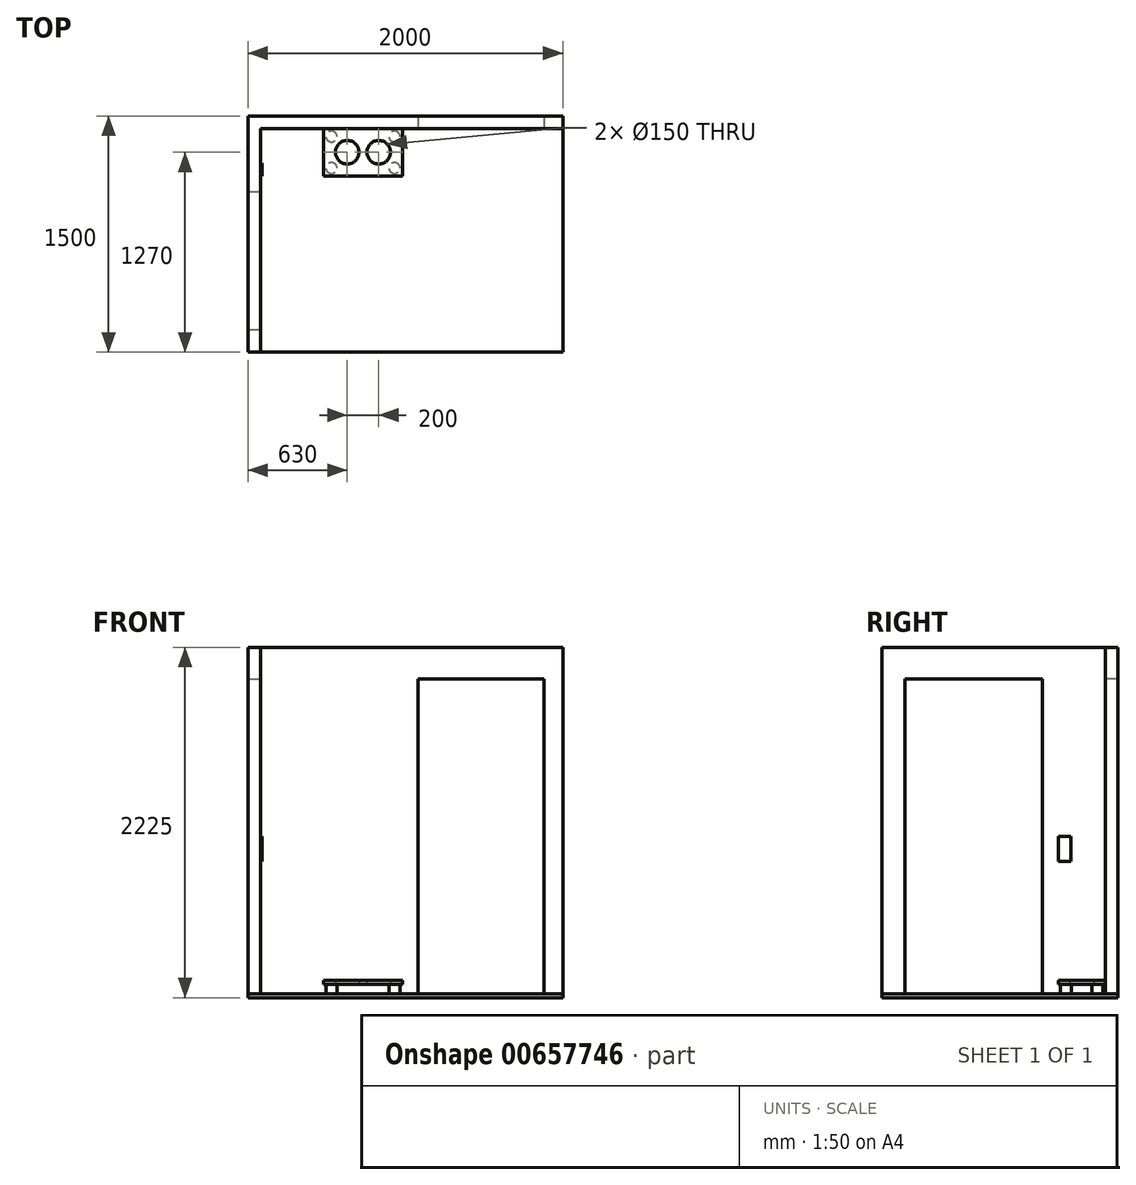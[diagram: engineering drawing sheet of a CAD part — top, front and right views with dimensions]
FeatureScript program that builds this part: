
annotation { "Feature Type Name" : "Feature", "Feature Type Description" : "" }
export const myFeature = defineFeature(function(context is Context, id is Id, definition is map)
    precondition{}
    {
        {
            var Q0;
            Q0=qCreatedBy(makeId("Top.planeOp"),FACE);
            var sketch = newSketch(context, id + "F0", { "sketchPlane" : qUnion([Q0])});
            skLineSegment(sketch, "E0.bottom", {"start": v(-1000, 1500) * mm, "end": v(1000, 1500) * mm});
            skLineSegment(sketch, "E0.top", {"start": v(-1000, 0) * mm, "end": v(1000, 0) * mm});
            skLineSegment(sketch, "E0.left", {"start": v(-1000, 1500) * mm, "end": v(-1000, 0) * mm});
            skLineSegment(sketch, "E0.right", {"start": v(1000, 1500) * mm, "end": v(1000, 0) * mm});
            skSolve(sketch);
        }
        {
            var Q0;
            Q0 = qSketchRegion(id + "F0", true);
            extrude(context, id + "F1", {"entities" : qUnion([Q0]), "depth" : 25 * mm, "offsetDistance" : 25 * mm});
        }
        {
            var Q0;
            Q0=makeQuery(id+"F1.opExtrude","CAP_FACE",FACE,{"disambiguationData":[OSD([sQuery(id+"F0.wireOp",EDGE,"E0.bottom"),sQuery(id+"F0.wireOp",EDGE,"E0.top"),sQuery(id+"F0.wireOp",EDGE,"E0.left"),sQuery(id+"F0.wireOp",EDGE,"E0.right")])],"isStart":false});
            var sketch = newSketch(context, id + "F2", { "sketchPlane" : qUnion([Q0])});
            skLineSegment(sketch, "E1", {"start": v(-1000, 0) * mm, "end": v(-1000, 1500) * mm});
            skLineSegment(sketch, "E2", {"start": v(-1000, 1500) * mm, "end": v(1000, 1500) * mm});
            skLineSegment(sketch, "E3", {"start": v(1000, 1500) * mm, "end": v(1000, 1420) * mm});
            skLineSegment(sketch, "E4", {"start": v(1000, 1420) * mm, "end": v(-920, 1420) * mm});
            skLineSegment(sketch, "E5", {"start": v(-920, 1420) * mm, "end": v(-920, 0) * mm});
            skLineSegment(sketch, "E6", {"start": v(-920, 0) * mm, "end": v(-1000, 0) * mm});
            skSolve(sketch);
        }
        {
            var Q0;
            Q0 = qSketchRegion(id + "F2", true);
            extrude(context, id + "F3", {"entities" : qUnion([Q0]), "depth" : 2200 * mm, "offsetDistance" : 25 * mm});
        }
        {
            var Q0;
            Q0=makeQuery(id+"F3.opExtrude","SWEPT_FACE",FACE,{"disambiguationData":[OSD([sQuery(id+"F2.wireOp",EDGE,"E5")])]});
            var sketch = newSketch(context, id + "F4", { "sketchPlane" : qUnion([Q0])});
            skLineSegment(sketch, "E7.bottom", {"start": v(1020, 25) * mm, "end": v(145, 25) * mm});
            skLineSegment(sketch, "E7.top", {"start": v(1020, 2025) * mm, "end": v(145, 2025) * mm});
            skLineSegment(sketch, "E7.left", {"start": v(1020, 25) * mm, "end": v(1020, 2025) * mm});
            skLineSegment(sketch, "E7.right", {"start": v(145, 25) * mm, "end": v(145, 2025) * mm});
            skSolve(sketch);
        }
        {
            var Q0;
            Q0 = qSketchRegion(id + "F4", true);
            extrude(context, id + "F5", {"entities" : qUnion([Q0]), "operationType" : NewBodyOperationType.REMOVE, "endBound" : BoundingType.THROUGH_ALL, "oppositeDirection" : true, "depth" : 25 * mm, "offsetDistance" : 25 * mm});
        }
        {
            var Q0;
            Q0=makeQuery(id+"F3.opExtrude","SWEPT_FACE",FACE,{"disambiguationData":[OSD([sQuery(id+"F2.wireOp",EDGE,"E4")])]});
            var sketch = newSketch(context, id + "F6", { "sketchPlane" : qUnion([Q0])});
            skLineSegment(sketch, "E8.bottom", {"start": v(80, 25) * mm, "end": v(880, 25) * mm});
            skLineSegment(sketch, "E8.top", {"start": v(80, 2025) * mm, "end": v(880, 2025) * mm});
            skLineSegment(sketch, "E8.left", {"start": v(80, 25) * mm, "end": v(80, 2025) * mm});
            skLineSegment(sketch, "E8.right", {"start": v(880, 25) * mm, "end": v(880, 2025) * mm});
            skSolve(sketch);
        }
        {
            var Q0;
            Q0 = qSketchRegion(id + "F6", true);
            extrude(context, id + "F7", {"entities" : qUnion([Q0]), "operationType" : NewBodyOperationType.REMOVE, "endBound" : BoundingType.THROUGH_ALL, "oppositeDirection" : true, "depth" : 25 * mm, "offsetDistance" : 25 * mm});
        }
        {
            var Q0;
            Q0=makeQuery(id+"F1.opExtrude","CAP_FACE",FACE,{"disambiguationData":[OSD([sQuery(id+"F0.wireOp",EDGE,"E0.bottom"),sQuery(id+"F0.wireOp",EDGE,"E0.top"),sQuery(id+"F0.wireOp",EDGE,"E0.left"),sQuery(id+"F0.wireOp",EDGE,"E0.right")])],"isStart":false});
            var sketch = newSketch(context, id + "F8", { "sketchPlane" : qUnion([Q0])});
            skCircle(sketch, "E9", {"center": v(-470, 1370) * mm, "radius": 35 * mm});
            skCircle(sketch, "E10", {"center": v(-470, 1170) * mm, "radius": 35 * mm});
            skCircle(sketch, "E11", {"center": v(-70, 1370) * mm, "radius": 35 * mm});
            skCircle(sketch, "E12", {"center": v(-70, 1170) * mm, "radius": 35 * mm});
            skLineSegment(sketch, "E13", {"start": v(-470, 1370) * mm, "end": v(-70, 1370) * mm, "construction": true});
            skLineSegment(sketch, "E14", {"start": v(-70, 1370) * mm, "end": v(-70, 1170) * mm, "construction": true});
            skLineSegment(sketch, "E15", {"start": v(-70, 1170) * mm, "end": v(-470, 1170) * mm, "construction": true});
            skLineSegment(sketch, "E16", {"start": v(-470, 1170) * mm, "end": v(-470, 1370) * mm, "construction": true});
            skSolve(sketch);
        }
        {
            var Q0;
            Q0 = qSketchRegion(id + "F8", true);
            extrude(context, id + "F9", {"entities" : qUnion([Q0]), "depth" : 60 * mm, "offsetDistance" : 25 * mm});
        }
        {
            var Q0;
            Q0=makeQuery(id+"F9.opExtrude","CAP_FACE",FACE,{"disambiguationData":[OSD([sQuery(id+"F8.wireOp",EDGE,"E10")])],"isStart":false});
            var sketch = newSketch(context, id + "F10", { "sketchPlane" : qUnion([Q0])});
            skLineSegment(sketch, "E17.bottom", {"start": v(-520, 1420) * mm, "end": v(-20, 1420) * mm});
            skLineSegment(sketch, "E17.top", {"start": v(-520, 1120) * mm, "end": v(-20, 1120) * mm});
            skLineSegment(sketch, "E17.left", {"start": v(-520, 1420) * mm, "end": v(-520, 1120) * mm});
            skLineSegment(sketch, "E17.right", {"start": v(-20, 1420) * mm, "end": v(-20, 1120) * mm});
            skCircle(sketch, "E18", {"center": v(-370, 1270) * mm, "radius": 75 * mm});
            skCircle(sketch, "E19", {"center": v(-170, 1270) * mm, "radius": 75 * mm});
            skSolve(sketch);
        }
        {
            var Q0;
            Q0 = qSketchRegion(id + "F10", true);
            extrude(context, id + "F11", {"entities" : qUnion([Q0]), "operationType" : NewBodyOperationType.ADD, "depth" : 25 * mm, "offsetDistance" : 25 * mm});
        }
        {
            var Q0;
            Q0=makeQuery(id+"F3.opExtrude","SWEPT_FACE",FACE,{"disambiguationData":[OSD([sQuery(id+"F2.wireOp",EDGE,"E5")])]});
            var sketch = newSketch(context, id + "F12", { "sketchPlane" : qUnion([Q0])});
            skLineSegment(sketch, "E20.bottom", {"start": v(1120, 1025) * mm, "end": v(1200, 1025) * mm});
            skLineSegment(sketch, "E20.top", {"start": v(1120, 865) * mm, "end": v(1200, 865) * mm});
            skLineSegment(sketch, "E20.left", {"start": v(1120, 1025) * mm, "end": v(1120, 865) * mm});
            skLineSegment(sketch, "E20.right", {"start": v(1200, 1025) * mm, "end": v(1200, 865) * mm});
            skSolve(sketch);
        }
        {
            var Q0;
            Q0 = qSketchRegion(id + "F12", true);
            extrude(context, id + "F13", {"entities" : qUnion([Q0]), "depth" : 10 * mm, "offsetDistance" : 25 * mm});
        }
    });
